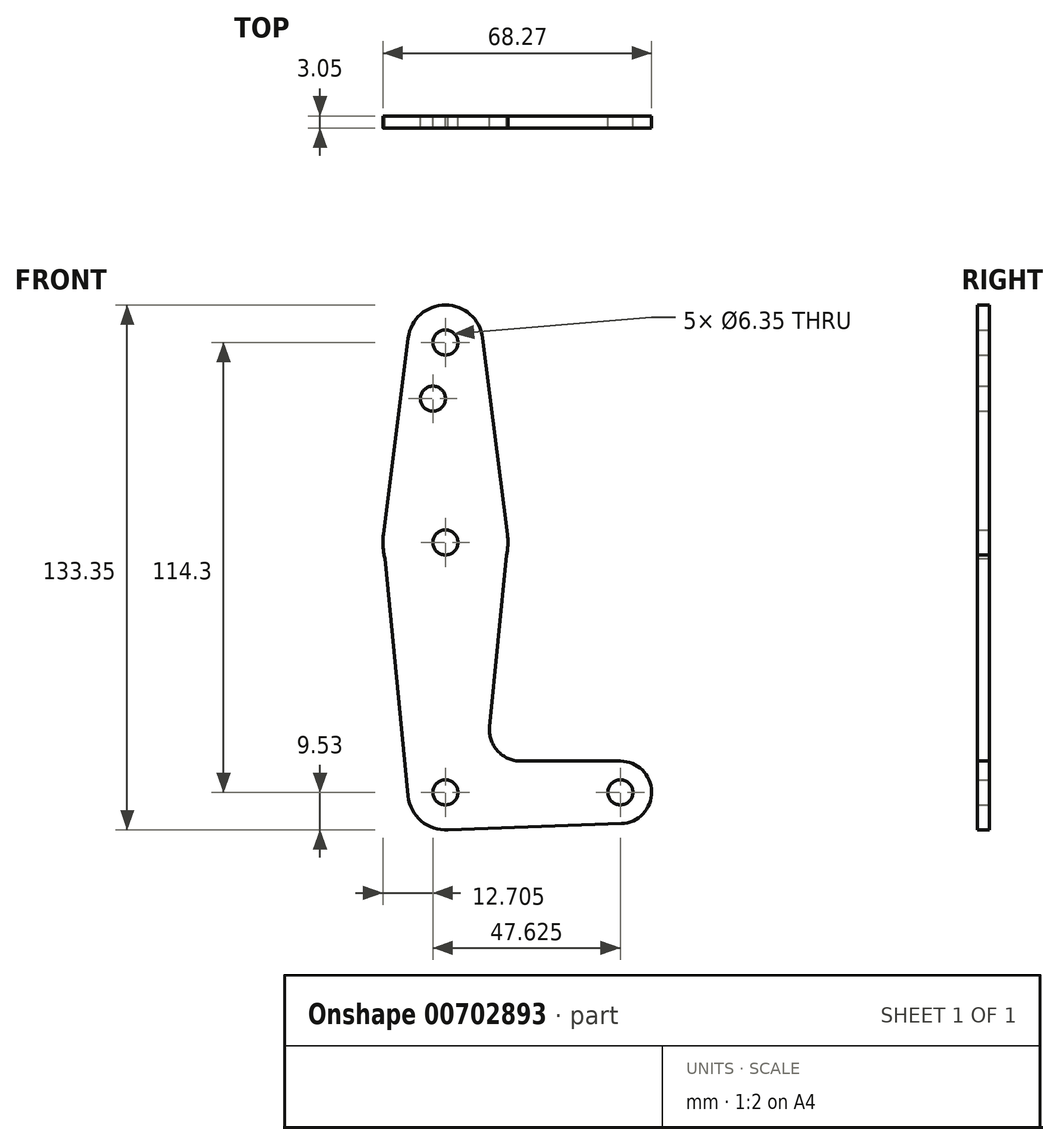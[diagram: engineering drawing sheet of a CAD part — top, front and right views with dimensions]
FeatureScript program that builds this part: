
annotation { "Feature Type Name" : "Feature", "Feature Type Description" : "" }
export const myFeature = defineFeature(function(context is Context, id is Id, definition is map)
    precondition{}
    {
        {
            var Q0;
            Q0=qCreatedBy(makeId("Front.planeOp"),FACE);
            var sketch = newSketch(context, id + "F0", { "sketchPlane" : qUnion([Q0])});
            skLineSegment(sketch, "E0", {"start": v(0, 50.8) * mm, "end": v(0, 0) * mm});
            skLineSegment(sketch, "E1", {"start": v(0, 0) * mm, "end": v(0, -63.5) * mm});
            skLineSegment(sketch, "E2", {"start": v(0, -63.5) * mm, "end": v(44.45, -63.5) * mm});
            skCircle(sketch, "E3", {"center": v(0, 50.8) * mm, "radius": 9.53 * mm});
            skCircle(sketch, "E4", {"center": v(0, -63.5) * mm, "radius": 9.53 * mm});
            skCircle(sketch, "E5", {"center": v(0, 0) * mm, "radius": 15.88 * mm});
            skCircle(sketch, "E6", {"center": v(44.45, -63.5) * mm, "radius": 7.94 * mm});
            skLineSegment(sketch, "E7", {"start": v(-9.45, 52) * mm, "end": v(-15.75, 1.98) * mm});
            skLineSegment(sketch, "E8", {"start": v(9.45, 52) * mm, "end": v(15.75, 1.98) * mm});
            skLineSegment(sketch, "E9", {"start": v(15.88, 0) * mm, "end": v(11.23, -46.83) * mm});
            skLineSegment(sketch, "E10", {"start": v(-15.75, 0) * mm, "end": v(-9.48, -64.42) * mm});
            skLineSegment(sketch, "E11", {"start": v(19.14, -55.56) * mm, "end": v(44.45, -55.56) * mm});
            skLineSegment(sketch, "E12", {"start": v(0, -73.03) * mm, "end": v(44.73, -71.43) * mm});
            skCircle(sketch, "E13", {"center": v(0, 50.8) * mm, "radius": 3.18 * mm});
            skCircle(sketch, "E14", {"center": v(0, 0) * mm, "radius": 3.18 * mm});
            skCircle(sketch, "E15", {"center": v(0, -63.5) * mm, "radius": 3.18 * mm});
            skCircle(sketch, "E16", {"center": v(44.45, -63.5) * mm, "radius": 3.18 * mm});
            skCircle(sketch, "E17", {"center": v(-3.17, 36.53) * mm, "radius": 3.18 * mm});
            skArc(sketch, "E18.filletArc", {"start": v(11.23, -46.83) * mm, "mid": v(13.25, -52.95) * mm, "end": v(19.14, -55.56) * mm});
            skSolve(sketch);
        }
        {
            var Q0;
            Q0 = qSketchRegion(id + "F0", true);
            var Q1;
            {var subQ0=sQuery(id+"F0.wireOp",EDGE,"E4");var subQ1=sQuery(id+"F0.wireOp",EDGE,"E1");var subQ2=makeQuery(id+"F0.imprint","INTERSECT",VERTEX,{"derivedFrom":[subQ1,subQ0]});Q1=makeQuery(id+"F0.imprint","IMPRINT",FACE,{"disambiguationData":[TD([[makeQuery(id+"F0.imprint","IMPRINT",EDGE,{"disambiguationData":[TD([[subQ2,-1.0]])],"derivedFrom":subQ1}),1.0]])]});}
            extrude(context, id + "F1", {"entities" : qUnion([Q0, Q1]), "depth" : 3.05 * mm, "offsetDistance" : 25.4 * mm});
        }
    });
